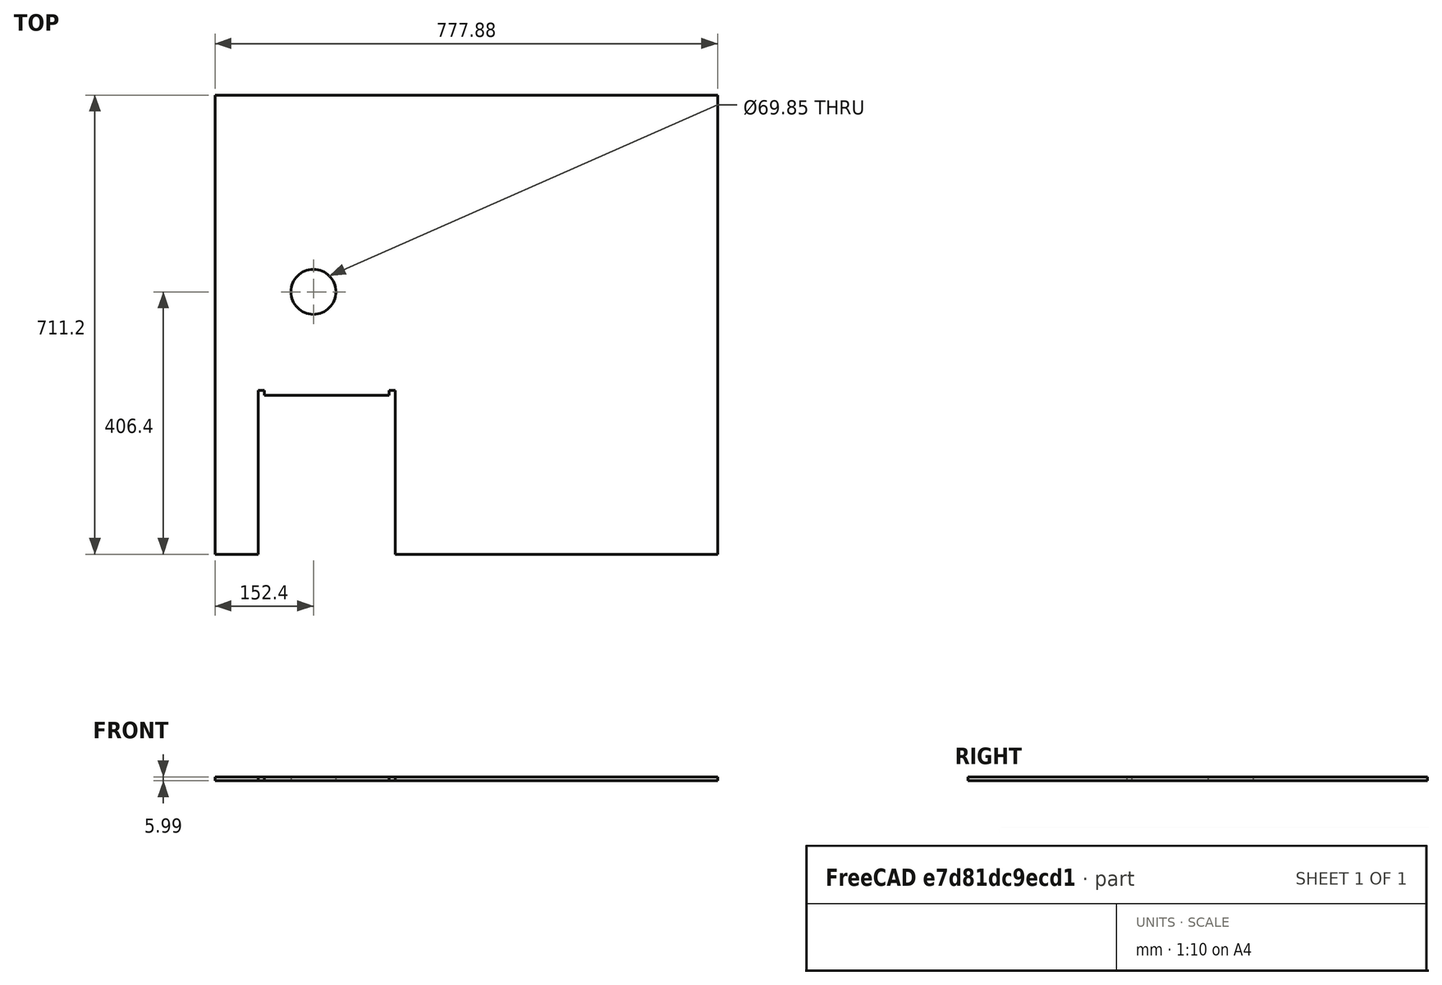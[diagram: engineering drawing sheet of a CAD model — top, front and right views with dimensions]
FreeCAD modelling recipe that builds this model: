
FCSTD DOCUMENT  (FreeCAD 0.19R24267 (Git))
Label: Inv1-P9
License: All rights reserved
LicenseURL: http://en.wikipedia.org/wiki/All_rights_reserved
objects: TechDraw::DrawViewDimension×13, TechDraw::DrawProjGroupItem×2, TechDraw::DrawHatch×2, TechDraw::DrawViewAnnotation×2, Sketcher::SketchObject×1, Part::Extrusion×1, TechDraw::DrawSVGTemplate×1, TechDraw::DrawProjGroup×1, TechDraw::DrawPage×1
note: 2 computed .brp shape members not serialized (recipe doc carries the construction recipe); baked Part::Feature solids carry a one-line shape summary decoded from their .brp

FEATURE [Sketcher::SketchObject] Sketch
  FullyConstrained = true
  sketch-geometry (13):
    g0: LineSegment StartX=0 StartY=0 StartZ=0 EndX=777.875 EndY=0 EndZ=0
    g1: LineSegment StartX=777.875 StartY=0 StartZ=0 EndX=777.875 EndY=-711.2 EndZ=0
    g2: LineSegment StartX=0 StartY=-711.2 StartZ=0 EndX=0 EndY=0 EndZ=0
    g3: Circle CenterX=152.4 CenterY=-304.8 CenterZ=0 NormalX=0 NormalY=0 NormalZ=1 AngleXU=0 Radius=34.925
    g4: LineSegment StartX=0 StartY=-711.2 StartZ=0 EndX=66.675 EndY=-711.2 EndZ=0
    g5: LineSegment StartX=66.675 StartY=-711.2 StartZ=0 EndX=66.675 EndY=-457.2 EndZ=0
    g6: LineSegment StartX=66.675 StartY=-457.2 StartZ=0 EndX=76.2 EndY=-457.2 EndZ=0
    g7: LineSegment StartX=76.2 StartY=-457.2 StartZ=0 EndX=76.2 EndY=-465.125 EndZ=0
    g8: LineSegment StartX=76.2 StartY=-465.125 StartZ=0 EndX=269.875 EndY=-465.125 EndZ=0
    g9: LineSegment StartX=269.875 StartY=-465.125 StartZ=0 EndX=269.875 EndY=-457.2 EndZ=0
    g10: LineSegment StartX=279.4 StartY=-457.2 StartZ=0 EndX=269.875 EndY=-457.2 EndZ=0
    g11: LineSegment StartX=279.4 StartY=-457.2 StartZ=0 EndX=279.4 EndY=-711.2 EndZ=0
    g12: LineSegment StartX=279.4 StartY=-711.2 StartZ=0 EndX=777.875 EndY=-711.2 EndZ=0
  constraints (38):
    c: Coincident(g0,g1)
    c: Coincident(g2,g0)
    c: Horizontal(g0)
    c: Vertical(g1)
    c: Vertical(g2)
    c: Coincident(g0,g-1)
    c: Distance(g0) = 777.875
    c: Distance(g1) = 711.2
    c: Diameter(g3) = 69.85
    c: Distance(g3,g0) = 304.8
    c: Distance(g3,g2) = 152.4
    c: Coincident(g4,g2)
    c: Horizontal(g4)
    c: Coincident(g5,g4)
    c: Vertical(g5)
    c: Coincident(g6,g5)
    c: Coincident(g7,g6)
    c: Coincident(g8,g7)
    c: Horizontal(g8)
    c: Coincident(g9,g8)
    c: Coincident(g10,g9)
    c: Horizontal(g10)
    c: Coincident(g11,g10)
    c: Vertical(g11)
    c: Coincident(g12,g1)
    c: Horizontal(g12)
    c: Coincident(g11,g12)
    c: Equal(g1,g2)
    c: Equal(g5,g11)
    c: Vertical(g7)
    c: Vertical(g9)
    c: Horizontal(g6)
    c: Distance(g11) = 254
    c: Distance(g8,g12) = 246.075
    c: Distance(g8) = 193.675
    c: Distance(g4,g11) = 212.725
    c: Distance(g4,g2) = 66.675
    c: Distance(g7,g5) = 9.525
FEATURE [Part::Extrusion] Extrude
  Base = -> Sketch
  Dir = (0,0,1)
  DirMode = 2
  FaceMakerClass = Part::FaceMakerBullseye
  LengthFwd = 5.9944
  LengthRev = 0
  Solid = true
  Symmetric = false
FEATURE [TechDraw::DrawSVGTemplate] Template
  Height = 215.9
  Orientation = 1
  Width = 279.4
FEATURE [TechDraw::DrawProjGroupItem] ProjItem  label="Front"
  CoarseView = false
  Direction = (0,0,1)
  Focus = 100
  HardHidden = false
  IsoCount = 0
  IsoHidden = false
  IsoVisible = false
  LockPosition = true
  Perspective = false
  Rotation = 0
  RotationVector = (1,0,0)
  Scale = 0.2
  ScaleType = 2
  SeamHidden = false
  SeamVisible = true
  SmoothHidden = false
  SmoothVisible = true
  Source = -> [Extrude]
  Type = 0
  X = 0
  XDirection = (1,0,0)
  Y = 0
FEATURE [TechDraw::DrawProjGroupItem] ProjItem001  label="Left"
  CoarseView = false
  Direction = (-1,0,1e-16)
  Focus = 100
  HardHidden = false
  IsoCount = 0
  IsoHidden = false
  IsoVisible = false
  LockPosition = false
  Perspective = false
  Rotation = 0
  RotationVector = (1,0,0)
  Scale = 0.2
  ScaleType = 2
  SeamHidden = false
  SeamVisible = true
  SmoothHidden = false
  SmoothVisible = true
  Source = -> [Extrude]
  Type = 1
  X = 107.645
  XDirection = (1e-16,0,1)
  Y = 0
FEATURE [TechDraw::DrawProjGroup] ProjGroup
  Anchor = -> ProjItem
  AutoDistribute = true
  LockPosition = false
  ProjectionType = 0
  Rotation = 0
  Scale = 0.2
  ScaleType = 2
  Source = -> [Extrude]
  Views = -> [ProjItem,ProjItem001]
  X = 126.214
  Y = 106.111
  spacingX = 15.0114
  spacingY = 15.0114
FEATURE [TechDraw::DrawHatch] Hatch  label="HatchF0"
  HatchPattern = <path>
  Source = -> ProjItem [Face0]
FEATURE [TechDraw::DrawHatch] Hatch001  label="Hatch001F0"
  HatchPattern = <path>
  Source = -> ProjItem001 [Face0]
FEATURE [TechDraw::DrawViewDimension] Dimension
  Arbitrary = false
  ArbitraryTolerances = false
  EqualTolerance = true
  FormatSpec = %.3f
  FormatSpecOverTolerance = %+.3f
  FormatSpecUnderTolerance = %+.3f
  Inverted = false
  LockPosition = false
  MeasureType = 1
  OverTolerance = 0
  References2D = -> [ProjItem]
  Rotation = 0
  ScaleType = 0
  TheoreticalExact = false
  Type = 1
  UnderTolerance = 0
  X = -1.67878
  Y = 83.543
FEATURE [TechDraw::DrawViewDimension] Dimension001
  Arbitrary = false
  ArbitraryTolerances = false
  EqualTolerance = true
  FormatSpec = %.3f
  FormatSpecOverTolerance = %+.3f
  FormatSpecUnderTolerance = %+.3f
  Inverted = false
  LockPosition = false
  MeasureType = 1
  OverTolerance = 0
  References2D = -> [ProjItem]
  Rotation = 0
  ScaleType = 0
  TheoreticalExact = false
  Type = 2
  UnderTolerance = 0
  X = 82.9171
  Y = 0
FEATURE [TechDraw::DrawViewDimension] Dimension002
  Arbitrary = false
  ArbitraryTolerances = false
  EqualTolerance = true
  FormatSpec = %.3f
  FormatSpecOverTolerance = %+.3f
  FormatSpecUnderTolerance = %+.3f
  Inverted = false
  LockPosition = false
  MeasureType = 1
  OverTolerance = 0
  References2D = -> [ProjItem001]
  Rotation = 0
  ScaleType = 0
  TheoreticalExact = false
  Type = 1
  UnderTolerance = 0
  X = 22.5068
  Y = 48.7751
FEATURE [TechDraw::DrawViewDimension] Dimension003
  Arbitrary = false
  ArbitraryTolerances = false
  EqualTolerance = true
  FormatSpec = %.3f
  FormatSpecOverTolerance = %+.3f
  FormatSpecUnderTolerance = %+.3f
  Inverted = false
  LockPosition = false
  MeasureType = 1
  OverTolerance = 0
  References2D = -> [ProjItem]
  Rotation = 0
  ScaleType = 0
  TheoreticalExact = false
  Type = 2
  UnderTolerance = 0
  X = -31.5567
  Y = 37.2344
FEATURE [TechDraw::DrawViewDimension] Dimension004
  Arbitrary = false
  ArbitraryTolerances = false
  EqualTolerance = true
  FormatSpec = %.3f
  FormatSpecOverTolerance = %+.3f
  FormatSpecUnderTolerance = %+.3f
  Inverted = false
  LockPosition = false
  MeasureType = 1
  OverTolerance = 0
  References2D = -> [ProjItem]
  Rotation = 0
  ScaleType = 0
  TheoreticalExact = false
  Type = 1
  UnderTolerance = 0
  X = -63.8342
  Y = 6.38326
FEATURE [TechDraw::DrawViewDimension] Dimension005
  Arbitrary = false
  ArbitraryTolerances = false
  EqualTolerance = true
  FormatSpec = ⌀%.3f
  FormatSpecOverTolerance = %+.3f
  FormatSpecUnderTolerance = %+.3f
  Inverted = false
  LockPosition = false
  MeasureType = 1
  OverTolerance = 0
  References2D = -> [ProjItem]
  Rotation = 0
  ScaleType = 0
  TheoreticalExact = false
  Type = 5
  UnderTolerance = 0
  X = -60.4549
  Y = 31.0404
FEATURE [TechDraw::DrawViewDimension] Dimension006
  Arbitrary = false
  ArbitraryTolerances = false
  EqualTolerance = true
  FormatSpec = %.3f
  FormatSpecOverTolerance = %+.3f
  FormatSpecUnderTolerance = %+.3f
  Inverted = false
  LockPosition = false
  MeasureType = 1
  OverTolerance = 0
  References2D = -> [ProjItem]
  Rotation = 0
  ScaleType = 0
  TheoreticalExact = false
  Type = 2
  UnderTolerance = 0
  X = -10.2493
  Y = -44.7485
FEATURE [TechDraw::DrawViewDimension] Dimension007
  Arbitrary = false
  ArbitraryTolerances = false
  EqualTolerance = true
  FormatSpec = %.3f
  FormatSpecOverTolerance = %+.3f
  FormatSpecUnderTolerance = %+.3f
  Inverted = false
  LockPosition = false
  MeasureType = 1
  OverTolerance = 0
  References2D = -> [ProjItem]
  Rotation = 0
  ScaleType = 0
  TheoreticalExact = false
  Type = 1
  UnderTolerance = 0
  X = -95.9872
  Y = -71.641
FEATURE [TechDraw::DrawViewDimension] Dimension008
  Arbitrary = false
  ArbitraryTolerances = false
  EqualTolerance = true
  FormatSpec = %.3f
  FormatSpecOverTolerance = %+.3f
  FormatSpecUnderTolerance = %+.3f
  Inverted = false
  LockPosition = false
  MeasureType = 1
  OverTolerance = 0
  References2D = -> [ProjItem]
  Rotation = 0
  ScaleType = 0
  TheoreticalExact = false
  Type = 1
  UnderTolerance = 0
  X = -41.2685
  Y = -77.1267
FEATURE [TechDraw::DrawViewDimension] Dimension009
  Arbitrary = false
  ArbitraryTolerances = false
  EqualTolerance = true
  FormatSpec = %.3f
  FormatSpecOverTolerance = %+.3f
  FormatSpecUnderTolerance = %+.3f
  Inverted = false
  LockPosition = false
  MeasureType = 1
  OverTolerance = 0
  References2D = -> [ProjItem]
  Rotation = 0
  ScaleType = 0
  TheoreticalExact = false
  Type = 2
  UnderTolerance = 0
  X = -53.1516
  Y = -6.56656
FEATURE [TechDraw::DrawViewDimension] Dimension010
  Arbitrary = false
  ArbitraryTolerances = false
  EqualTolerance = true
  FormatSpec = %.3f
  FormatSpecOverTolerance = %+.3f
  FormatSpecUnderTolerance = %+.3f
  Inverted = false
  LockPosition = false
  MeasureType = 1
  OverTolerance = 0
  References2D = -> [ProjItem]
  Rotation = 0
  ScaleType = 0
  TheoreticalExact = false
  Type = 2
  UnderTolerance = 0
  X = -40.2011
  Y = -6.50014
FEATURE [TechDraw::DrawViewDimension] Dimension011
  Arbitrary = false
  ArbitraryTolerances = false
  EqualTolerance = true
  FormatSpec = %.3f
  FormatSpecOverTolerance = %+.3f
  FormatSpecUnderTolerance = %+.3f
  Inverted = false
  LockPosition = false
  MeasureType = 1
  OverTolerance = 0
  References2D = -> [ProjItem]
  Rotation = 0
  ScaleType = 0
  TheoreticalExact = false
  Type = 1
  UnderTolerance = 0
  X = -71.8028
  Y = -10.5271
FEATURE [TechDraw::DrawViewDimension] Dimension012
  Arbitrary = false
  ArbitraryTolerances = false
  EqualTolerance = true
  FormatSpec = %.3f
  FormatSpecOverTolerance = %+.3f
  FormatSpecUnderTolerance = %+.3f
  Inverted = false
  LockPosition = false
  MeasureType = 1
  OverTolerance = 0
  References2D = -> [ProjItem]
  Rotation = 0
  ScaleType = 0
  TheoreticalExact = false
  Type = 1
  UnderTolerance = 0
  X = -9.17931
  Y = -11.3245
FEATURE [TechDraw::DrawViewAnnotation] Annotation
  Font = osifont
  LineSpace = 80
  LockPosition = false
  MaxWidth = -1
  Rotation = 0
  ScaleType = 0
  Text = Figure S1 (Inverted 1) | Panel 9 [right side exterior baffle] | Quantity: 1
  TextSize = 5.0038
  TextStyle = 0
  X = 47.6094
  Y = 195.58
FEATURE [TechDraw::DrawViewAnnotation] Annotation002
  Font = osifont
  LineSpace = 80
  LockPosition = false
  MaxWidth = -1
  Rotation = 0
  ScaleType = 0
  Text = Units: Inches
  TextSize = 5.0038
  TextStyle = 0
  X = 259.08
  Y = 5.08
FEATURE [TechDraw::DrawPage] Page
  KeepUpdated = true
  NextBalloonIndex = 1
  ProjectionType = 0
  Template = -> Template
  Views = -> [ProjGroup,Dimension,Dimension001,Dimension002,Dimension003,Dimension004,Dimension005,Dimension006,Dimension007,Dimension008,Dimension009,Dimension010,Dimension011,Dimension012,Annotation,Annotation002]
note: 2 file-system paths scrubbed to <path> (originals preserved in the JSON sidecar)
